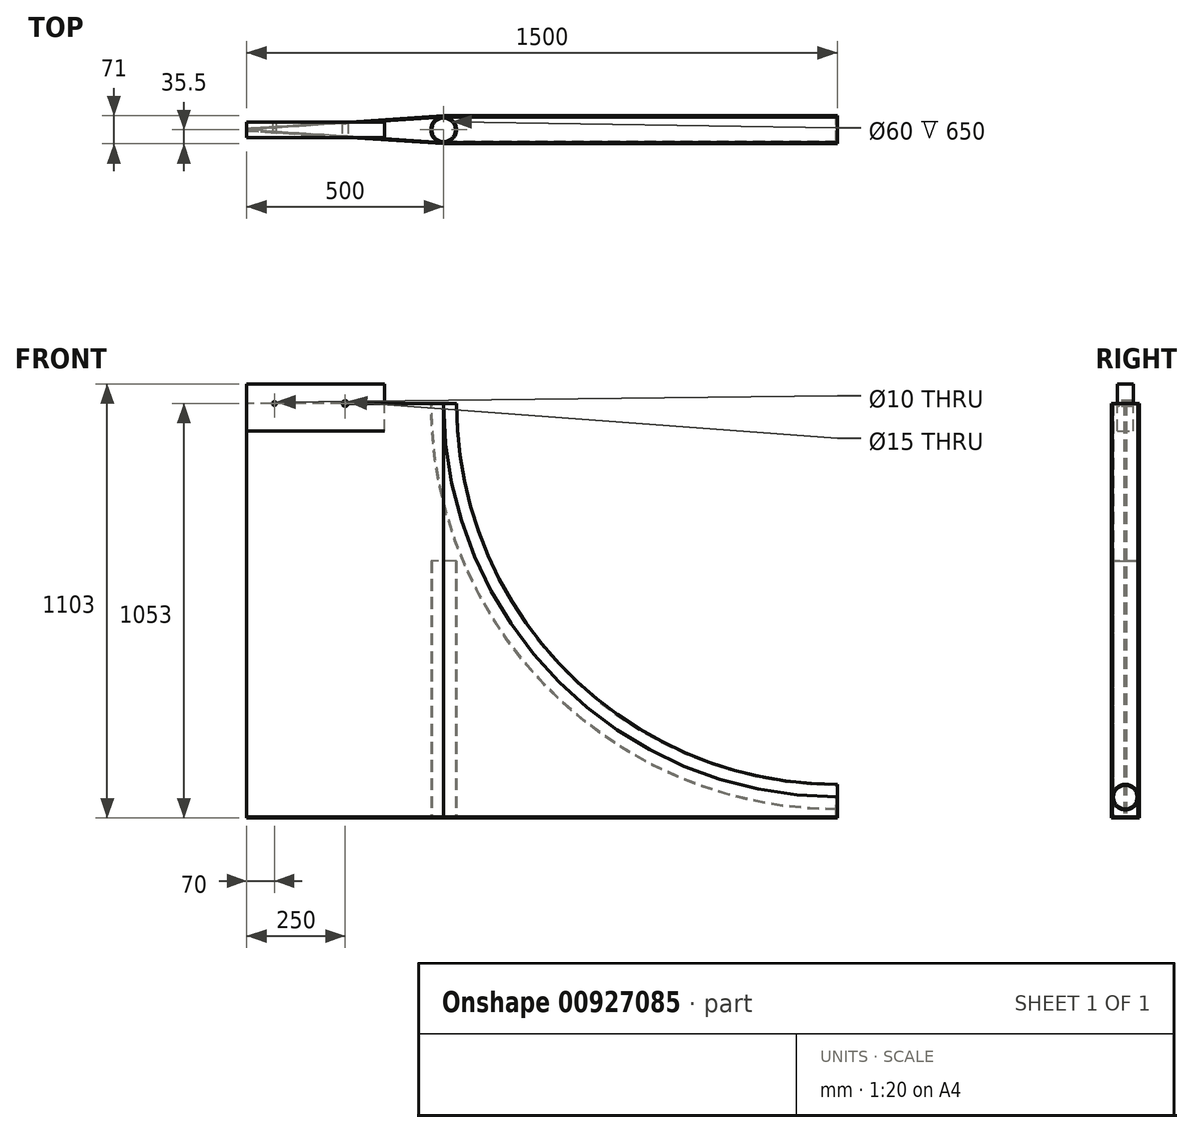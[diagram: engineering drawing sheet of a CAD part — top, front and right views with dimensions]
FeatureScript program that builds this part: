
annotation { "Feature Type Name" : "Feature", "Feature Type Description" : "" }
export const myFeature = defineFeature(function(context is Context, id is Id, definition is map)
    precondition{}
    {
        {
            var Q0;
            Q0=qCreatedBy(makeId("Front.planeOp"),FACE);
            var sketch = newSketch(context, id + "F0", { "sketchPlane" : qUnion([Q0])});
            skCircle(sketch, "E0", {"center": v(0, 0) * mm, "radius": 7.5 * mm});
            skCircle(sketch, "E1", {"center": v(-180, 0) * mm, "radius": 5 * mm});
            skArc(sketch, "E2", {"start": v(250, 0) * mm, "mid": v(542.9, -707.1) * mm, "end": v(1250, -1000) * mm});
            skLineSegment(sketch, "E3", {"start": v(250, 0) * mm, "end": v(250, -1050) * mm});
            skLineSegment(sketch, "E4", {"start": v(250, -1050) * mm, "end": v(1250, -1050) * mm});
            skLineSegment(sketch, "E5", {"start": v(1250, -1050) * mm, "end": v(1250, -1050) * mm});
            skLineSegment(sketch, "E6", {"start": v(1250, -1000) * mm, "end": v(1250, -1050) * mm});
            skSolve(sketch);
        }
        {
            var Q0;
            Q0=qCreatedBy(makeId("Top.planeOp"),FACE);
            var sketch = newSketch(context, id + "F1", { "sketchPlane" : qUnion([Q0])});
            skCircle(sketch, "E7", {"center": v(250, 0) * mm, "radius": 30 * mm});
            skCircle(sketch, "E8", {"center": v(250, 0) * mm, "radius": 32.5 * mm});
            skSolve(sketch);
        }
        {
            var Q0;
            Q0 = qSketchRegion(id + "F1", true);
            var Q1;
            Q1=sQuery(id+"F0.wireOp",EDGE,"E2");
            sweep(context, id + "F2", {"profiles" : qUnion([Q0]), "path" : qUnion([Q1])});
        }
        {
            var Q0;
            Q0=qCreatedBy(makeId("Front.planeOp"),FACE);
            var sketch = newSketch(context, id + "F3", { "sketchPlane" : qUnion([Q0])});
            skLineSegment(sketch, "E9.bottom", {"start": v(100, -70) * mm, "end": v(-250, -70) * mm});
            skLineSegment(sketch, "E9.top", {"start": v(100, 50) * mm, "end": v(-250, 50) * mm});
            skLineSegment(sketch, "E9.left", {"start": v(100, -70) * mm, "end": v(100, 50) * mm});
            skLineSegment(sketch, "E9.right", {"start": v(-250, -70) * mm, "end": v(-250, 50) * mm});
            skSolve(sketch);
        }
        {
            var Q0;
            Q0=makeQuery(id+"F2.opSweep","CAP_FACE",FACE,{"disambiguationData":[OSD([sQuery(id+"F0.wireOp",VERTEX,"E2.start"),sQuery(id+"F1.wireOp",EDGE,"E7"),sQuery(id+"F1.wireOp",EDGE,"E8")])],"isStart":true});
            var sketch = newSketch(context, id + "F4", { "sketchPlane" : qUnion([Q0])});
            skLineSegment(sketch, "E10", {"start": v(250, 0) * mm, "end": v(250, 32.5) * mm, "construction": true});
            skLineSegment(sketch, "E11", {"start": v(250, 32.5) * mm, "end": v(-250, 0) * mm});
            skSolve(sketch);
        }
        {
            var Q0;
            Q0=sQuery(id+"F4.wireOp",EDGE,"E11");
            extrude(context, id + "F5", {"bodyType" : ToolBodyType.SURFACE, "surfaceEntities" : qUnion([Q0]), "oppositeDirection" : true, "depth" : 1050 * mm, "offsetDistance" : 25 * mm});
        }
        {
            var Q0;
            Q0=makeQuery(id+"F3.imprint","IMPRINT",FACE,{"disambiguationData":[TD([[makeQuery(id+"F3.imprint","IMPRINT",EDGE,{"derivedFrom":sQuery(id+"F3.wireOp",EDGE,"E9.bottom")}),-1.0]])]});
            extrude(context, id + "F6", {"entities" : qUnion([Q0]), "endBound" : BoundingType.SYMMETRIC, "depth" : 40 * mm, "offsetDistance" : 25 * mm});
        }
        {
            var Q0;
            Q0=qCreatedBy(makeId("Front.planeOp"),FACE);
            cPlane(context, id + "F7", {"entities" : qUnion([Q0]), "cplaneType" : CPlaneType.OFFSET, "offset" : 32.5 * mm, "oppositeDirection" : true, "width" : 150 * mm, "height" : 150 * mm});
        }
        {
            var Q0;
            Q0=qCreatedBy(id+"F7.planeOp",FACE);
            var sketch = newSketch(context, id + "F8", { "sketchPlane" : qUnion([Q0])});
            skLineSegment(sketch, "E12", {"start": v(1250, -1050) * mm, "end": v(250, -1050) * mm});
            skLineSegment(sketch, "E13", {"start": v(1250, -1050) * mm, "end": v(1250, -1000) * mm});
            skLineSegment(sketch, "E14", {"start": v(250, -1050) * mm, "end": v(250, 0) * mm});
            skArc(sketch, "E15", {"start": v(250, 0) * mm, "mid": v(542.9, -707.1) * mm, "end": v(1250, -1000) * mm});
            skSolve(sketch);
        }
        {
            var Q0;
            Q0=makeQuery(id+"F8.imprint","IMPRINT",FACE,{"disambiguationData":[TD([[makeQuery(id+"F8.imprint","IMPRINT",EDGE,{"derivedFrom":sQuery(id+"F8.wireOp",EDGE,"E12")}),-1.0]])]});
            var Q1;
            Q1=makeQuery(id+"F5.opExtrude","SWEPT_FACE",FACE,{"disambiguationData":[OSD([sQuery(id+"F4.wireOp",EDGE,"E11")])]});
            extrude(context, id + "F9", {"entities" : qUnion([Q0, Q1]), "oppositeDirection" : true, "depth" : 3 * mm, "offsetDistance" : 25 * mm});
        }
        {
            var Q0;
            Q0=makeQuery(id+"F9.opExtrude","SWEPT_BODY",BODY,{"disambiguationData":[OSD([sQuery(id+"F8.wireOp",EDGE,"E12"),sQuery(id+"F8.wireOp",EDGE,"E13"),sQuery(id+"F8.wireOp",EDGE,"E14"),sQuery(id+"F8.wireOp",EDGE,"E15")])]});
            var Q1;
            Q1=makeQuery(id+"F9.opExtrude","SWEPT_BODY",BODY,{"disambiguationData":[OSD([sQuery(id+"F4.wireOp",EDGE,"E11")])]});
            var Q2;
            Q2=qCreatedBy(makeId("Front.planeOp"),FACE);
            mirror(context, id + "F10", {"entities" : qUnion([Q0, Q1]), "mirrorPlane" : qUnion([Q2])});
        }
        {
            var Q0;
            Q0=makeQuery(id+"F9.opExtrude","SWEPT_FACE",FACE,{"disambiguationData":[OSD([sQuery(id+"F8.wireOp",EDGE,"E13")])]});
            var sketch = newSketch(context, id + "F11", { "sketchPlane" : qUnion([Q0])});
            skLineSegment(sketch, "E16", {"start": v(32.5, -1000) * mm, "end": v(32.5, -1050) * mm});
            skLineSegment(sketch, "E17", {"start": v(32.5, -1050) * mm, "end": v(-32.5, -1050) * mm});
            skLineSegment(sketch, "E18", {"start": v(-32.5, -1050) * mm, "end": v(-32.5, -1000) * mm});
            skArc(sketch, "E19", {"start": v(-32.5, -1000) * mm, "mid": v(0, -1032.5) * mm, "end": v(32.5, -1000) * mm});
            skSolve(sketch);
        }
        {
            var Q0;
            Q0 = qSketchRegion(id + "F11", true);
            extrude(context, id + "F12", {"entities" : qUnion([Q0]), "oppositeDirection" : true, "depth" : 3 * mm, "offsetDistance" : 25 * mm});
        }
        {
            var Q0;
            Q0=makeQuery(id+"F9.opExtrude","SWEPT_FACE",FACE,{"disambiguationData":[OSD([sQuery(id+"F8.wireOp",EDGE,"E12")])]});
            var sketch = newSketch(context, id + "F13", { "sketchPlane" : qUnion([Q0])});
            skLineSegment(sketch, "E20", {"start": v(1250, -35.5) * mm, "end": v(250, -35.5) * mm});
            skLineSegment(sketch, "E21", {"start": v(250, -35.5) * mm, "end": v(-250, -3) * mm});
            skLineSegment(sketch, "E22", {"start": v(250, 35.5) * mm, "end": v(1250, 35.5) * mm});
            skLineSegment(sketch, "E23", {"start": v(1250, 35.5) * mm, "end": v(1250, -35.5) * mm});
            skLineSegment(sketch, "E24", {"start": v(-250, -3) * mm, "end": v(-250, 3) * mm});
            skLineSegment(sketch, "E25", {"start": v(-250, 3) * mm, "end": v(250, 35.5) * mm});
            skSolve(sketch);
        }
        {
            var Q0;
            Q0 = qSketchRegion(id + "F13", true);
            extrude(context, id + "F14", {"entities" : qUnion([Q0]), "depth" : 3 * mm, "offsetDistance" : 25 * mm});
        }
        {
            var Q0;
            Q0=makeQuery(id+"F2.opSweep","CAP_FACE",FACE,{"disambiguationData":[OSD([sQuery(id+"F0.wireOp",VERTEX,"E2.start"),sQuery(id+"F1.wireOp",EDGE,"E7"),sQuery(id+"F1.wireOp",EDGE,"E8")])],"isStart":true});
            var sketch = newSketch(context, id + "F15", { "sketchPlane" : qUnion([Q0])});
            skSolve(sketch);
        }
        {
            var Q0;
            {var subQ0=sQuery(id+"F0.wireOp",VERTEX,"E2.start");Q0=makeQuery(id+"F15.imprint","IMPRINT",FACE,{"disambiguationData":[TD([[makeQuery(id+"F15.imprint","IMPRINT",EDGE,{"derivedFrom":makeQuery(id+"F2.opSweep","CAP_EDGE",EDGE,{"disambiguationData":[OSD([subQ0,sQuery(id+"F1.wireOp",EDGE,"E7")])],"isStart":true})}),-1.0]])]});}
            var sketch = newSketch(context, id + "F16", { "sketchPlane" : qUnion([Q0])});
            skArc(sketch, "E26", {"start": v(250, 32.5) * mm, "mid": v(217.5, 0) * mm, "end": v(250, -32.5) * mm});
            skLineSegment(sketch, "E27", {"start": v(250, -32.5) * mm, "end": v(100, -22.75) * mm});
            skLineSegment(sketch, "E28", {"start": v(100, -22.75) * mm, "end": v(100, 22.75) * mm});
            skLineSegment(sketch, "E29", {"start": v(100, 22.75) * mm, "end": v(250, 32.5) * mm});
            skSolve(sketch);
        }
        {
            var Q0;
            Q0 = qSketchRegion(id + "F16", true);
            extrude(context, id + "F17", {"entities" : qUnion([Q0]), "oppositeDirection" : true, "depth" : 3 * mm, "offsetDistance" : 25 * mm});
        }
        {
            var Q0;
            Q0=makeQuery(id+"F0.imprint","IMPRINT",FACE,{"disambiguationData":[TD([[makeQuery(id+"F0.imprint","IMPRINT",EDGE,{"derivedFrom":sQuery(id+"F0.wireOp",EDGE,"E0")}),1.0]])]});
            var Q1;
            Q1=makeQuery(id+"F0.imprint","IMPRINT",FACE,{"disambiguationData":[TD([[makeQuery(id+"F0.imprint","IMPRINT",EDGE,{"derivedFrom":sQuery(id+"F0.wireOp",EDGE,"E1")}),1.0]])]});
            var Q2;
            Q2=sQuery(id+"F0.wireOp",EDGE,"E1");
            var Q3;
            Q3=sQuery(id+"F0.wireOp",EDGE,"E0");
            extrude(context, id + "F18", {"entities" : qUnion([Q0, Q1]), "operationType" : NewBodyOperationType.REMOVE, "surfaceEntities" : qUnion([Q2, Q3]), "endBound" : BoundingType.THROUGH_ALL, "oppositeDirection" : true, "depth" : 25 * mm, "offsetDistance" : 25 * mm, "hasSecondDirection" : true, "secondDirectionBound" : SecondDirectionBoundingType.THROUGH_ALL, "secondDirectionOppositeDirection" : false, "secondDirectionDepth" : 25 * mm});
        }
        {
            var Q0;
            Q0=makeQuery(id+"F14.opExtrude","CAP_FACE",FACE,{"disambiguationData":[OSD([sQuery(id+"F13.wireOp",EDGE,"E20"),sQuery(id+"F13.wireOp",EDGE,"E21"),sQuery(id+"F13.wireOp",EDGE,"E22"),sQuery(id+"F13.wireOp",EDGE,"E23"),sQuery(id+"F13.wireOp",EDGE,"E24"),sQuery(id+"F13.wireOp",EDGE,"E25")])],"isStart":true});
            var sketch = newSketch(context, id + "F19", { "sketchPlane" : qUnion([Q0])});
            skCircle(sketch, "E30", {"center": v(250, 0) * mm, "radius": 32.5 * mm});
            skCircle(sketch, "E31", {"center": v(250, 0) * mm, "radius": 30 * mm});
            skSolve(sketch);
        }
        {
            var Q0;
            Q0 = qSketchRegion(id + "F19", true);
            extrude(context, id + "F20", {"entities" : qUnion([Q0]), "depth" : 650 * mm, "offsetDistance" : 25 * mm});
        }
    });
